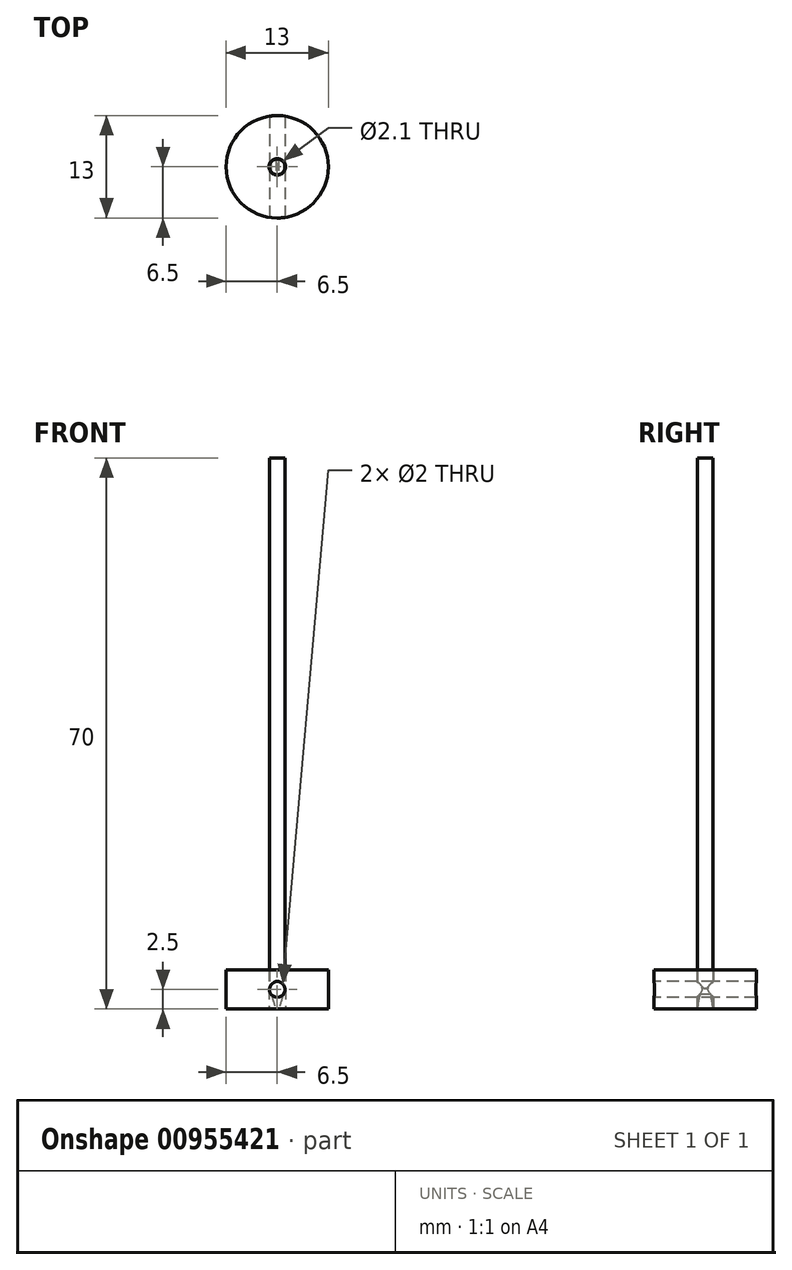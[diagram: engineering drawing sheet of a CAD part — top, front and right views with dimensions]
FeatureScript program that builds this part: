
annotation { "Feature Type Name" : "Feature", "Feature Type Description" : "" }
export const myFeature = defineFeature(function(context is Context, id is Id, definition is map)
    precondition{}
    {
        {
            var Q0;
            Q0=qCreatedBy(makeId("Top.planeOp"),FACE);
            var sketch = newSketch(context, id + "F0", { "sketchPlane" : qUnion([Q0])});
            skCircle(sketch, "E0", {"center": v(0, 0) * mm, "radius": 1 * mm});
            skSolve(sketch);
        }
        {
            var Q0;
            Q0 = qSketchRegion(id + "F0", true);
            extrude(context, id + "F1", {"entities" : qUnion([Q0]), "depth" : 70 * mm, "offsetDistance" : 25 * mm});
        }
        {
            var Q0;
            Q0=qCreatedBy(makeId("Front.planeOp"),FACE);
            var sketch = newSketch(context, id + "F2", { "sketchPlane" : qUnion([Q0])});
            skLineSegment(sketch, "E1", {"start": v(0.19, 0) * mm, "end": v(1.15, 3.1) * mm});
            skLineSegment(sketch, "E2", {"start": v(1.15, 3.1) * mm, "end": v(1.15, 0) * mm});
            skLineSegment(sketch, "E3", {"start": v(1.15, 0) * mm, "end": v(0.19, 0) * mm});
            skLineSegment(sketch, "E4.MirrorCS", {"start": v(-0.19, 0) * mm, "end": v(-1.15, 3.1) * mm});
            skLineSegment(sketch, "E5.MirrorCS", {"start": v(-1.15, 3.1) * mm, "end": v(-1.15, 0) * mm});
            skLineSegment(sketch, "E6.MirrorCS", {"start": v(-1.15, 0) * mm, "end": v(-0.19, 0) * mm});
            skSolve(sketch);
        }
        {
            var Q0;
            Q0 = qSketchRegion(id + "F2", true);
            extrude(context, id + "F3", {"entities" : qUnion([Q0]), "operationType" : NewBodyOperationType.REMOVE, "endBound" : BoundingType.SYMMETRIC, "oppositeDirection" : true, "depth" : 25 * mm, "offsetDistance" : 25 * mm});
        }
        {
            var Q0;
            Q0=qCreatedBy(makeId("Top.planeOp"),FACE);
            var sketch = newSketch(context, id + "F4", { "sketchPlane" : qUnion([Q0])});
            skCircle(sketch, "E7", {"center": v(0, 0) * mm, "radius": 1.05 * mm});
            skCircle(sketch, "E8", {"center": v(0, 0) * mm, "radius": 6.5 * mm});
            skSolve(sketch);
        }
        {
            var Q0;
            Q0 = qSketchRegion(id + "F4", true);
            extrude(context, id + "F5", {"entities" : qUnion([Q0]), "depth" : 5 * mm, "offsetDistance" : 25 * mm});
        }
        {
            var Q0;
            Q0=qCreatedBy(makeId("Front.planeOp"),FACE);
            var sketch = newSketch(context, id + "F6", { "sketchPlane" : qUnion([Q0])});
            skCircle(sketch, "E9", {"center": v(0, 2.5) * mm, "radius": 1 * mm});
            skSolve(sketch);
        }
        {
            var Q0;
            Q0 = qSketchRegion(id + "F6", true);
            extrude(context, id + "F7", {"entities" : qUnion([Q0]), "operationType" : NewBodyOperationType.REMOVE, "endBound" : BoundingType.SYMMETRIC, "oppositeDirection" : true, "depth" : 25 * mm, "offsetDistance" : 25 * mm});
        }
    });
